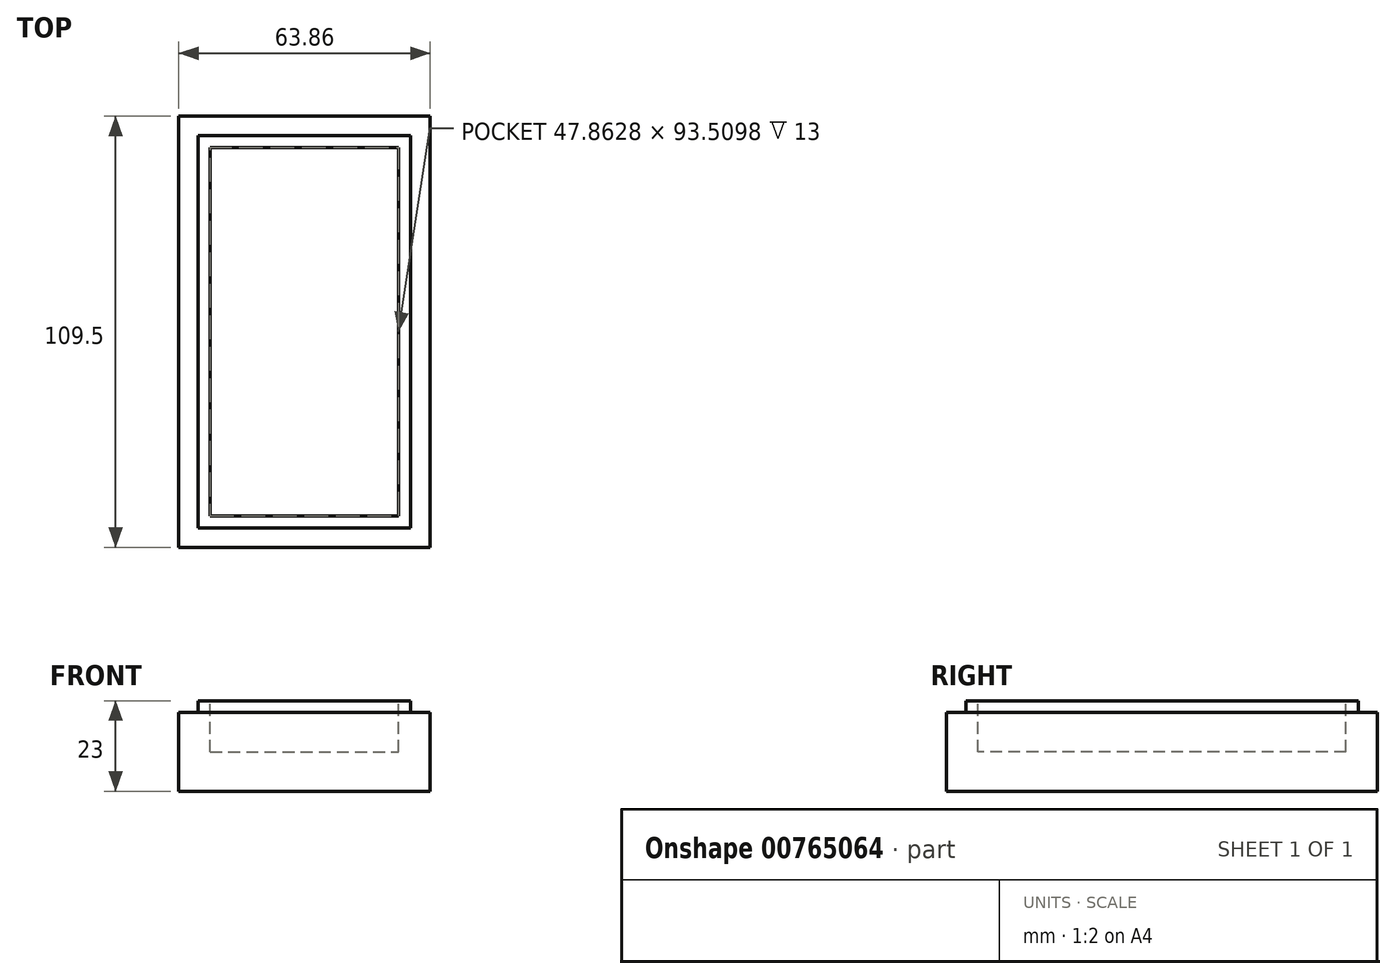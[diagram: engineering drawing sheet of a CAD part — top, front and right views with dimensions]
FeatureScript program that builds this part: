
annotation { "Feature Type Name" : "Feature", "Feature Type Description" : "" }
export const myFeature = defineFeature(function(context is Context, id is Id, definition is map)
    precondition{}
    {
        {
            var Q0;
            Q0=qCreatedBy(makeId("Top.planeOp"),FACE);
            var sketch = newSketch(context, id + "F0", { "sketchPlane" : qUnion([Q0])});
            skLineSegment(sketch, "E0.bottom", {"start": v(-31.93, 54.75) * mm, "end": v(31.93, 54.75) * mm});
            skLineSegment(sketch, "E0.top", {"start": v(-31.93, -54.75) * mm, "end": v(31.93, -54.75) * mm});
            skLineSegment(sketch, "E0.left", {"start": v(-31.93, 54.75) * mm, "end": v(-31.93, -54.75) * mm});
            skLineSegment(sketch, "E0.right", {"start": v(31.93, 54.75) * mm, "end": v(31.93, -54.75) * mm});
            skPoint(sketch, "E0.middle", {"position": v(0, 0) * mm});
            skSolve(sketch);
        }
        {
            var Q0;
            Q0=makeQuery(id+"F0.imprint","IMPRINT",FACE,{"disambiguationData":[TD([[makeQuery(id+"F0.imprint","IMPRINT",EDGE,{"derivedFrom":sQuery(id+"F0.wireOp",EDGE,"E0.bottom")}),-1.0]])]});
            extrude(context, id + "F1", {"entities" : qUnion([Q0]), "depth" : 20 * mm, "offsetDistance" : 25 * mm});
        }
        {
            var Q0;
            Q0=makeQuery(id+"F1.opExtrude","CAP_FACE",FACE,{"disambiguationData":[OSD([sQuery(id+"F0.wireOp",EDGE,"E0.bottom"),sQuery(id+"F0.wireOp",EDGE,"E0.top"),sQuery(id+"F0.wireOp",EDGE,"E0.left"),sQuery(id+"F0.wireOp",EDGE,"E0.right")])],"isStart":false});
            var sketch = newSketch(context, id + "F2", { "sketchPlane" : qUnion([Q0])});
            skLineSegment(sketch, "E1.0", {"start": v(-23.93, 46.75) * mm, "end": v(-23.93, -46.75) * mm});
            skLineSegment(sketch, "E1.1", {"start": v(-23.93, 46.75) * mm, "end": v(23.93, 46.75) * mm});
            skLineSegment(sketch, "E1.2", {"start": v(23.93, 46.75) * mm, "end": v(23.93, -46.75) * mm});
            skLineSegment(sketch, "E1.3", {"start": v(-23.93, -46.75) * mm, "end": v(23.93, -46.75) * mm});
            skSolve(sketch);
        }
        {
            var Q0;
            Q0=makeQuery(id+"F2.imprint","IMPRINT",FACE,{"disambiguationData":[TD([[makeQuery(id+"F2.imprint","IMPRINT",EDGE,{"derivedFrom":sQuery(id+"F2.wireOp",EDGE,"E1.0")}),1.0]])]});
            extrude(context, id + "F3", {"entities" : qUnion([Q0]), "operationType" : NewBodyOperationType.REMOVE, "oppositeDirection" : true, "depth" : 10 * mm, "offsetDistance" : 25 * mm});
        }
        {
            var Q0;
            Q0=makeQuery(id+"F1.opExtrude","CAP_FACE",FACE,{"disambiguationData":[OSD([sQuery(id+"F0.wireOp",EDGE,"E0.bottom"),sQuery(id+"F0.wireOp",EDGE,"E0.top"),sQuery(id+"F0.wireOp",EDGE,"E0.left"),sQuery(id+"F0.wireOp",EDGE,"E0.right")])],"isStart":false});
            var sketch = newSketch(context, id + "F4", { "sketchPlane" : qUnion([Q0])});
            skLineSegment(sketch, "E2.bottom", {"start": v(-27, 49.83) * mm, "end": v(27, 49.83) * mm});
            skLineSegment(sketch, "E2.top", {"start": v(-27, -49.83) * mm, "end": v(27, -49.83) * mm});
            skLineSegment(sketch, "E2.left", {"start": v(-27, 49.83) * mm, "end": v(-27, -49.83) * mm});
            skLineSegment(sketch, "E2.right", {"start": v(27, 49.83) * mm, "end": v(27, -49.83) * mm});
            skPoint(sketch, "E2.middle", {"position": v(0, 0) * mm});
            skSolve(sketch);
        }
        {
            var Q0;
            Q0=makeQuery(id+"F4.imprint","IMPRINT",FACE,{"disambiguationData":[TD([[makeQuery(id+"F4.imprint","IMPRINT",EDGE,{"derivedFrom":sQuery(id+"F4.wireOp",EDGE,"E2.bottom")}),-1.0]])]});
            extrude(context, id + "F5", {"entities" : qUnion([Q0]), "operationType" : NewBodyOperationType.ADD, "depth" : 3 * mm, "offsetDistance" : 25 * mm});
        }
    });
